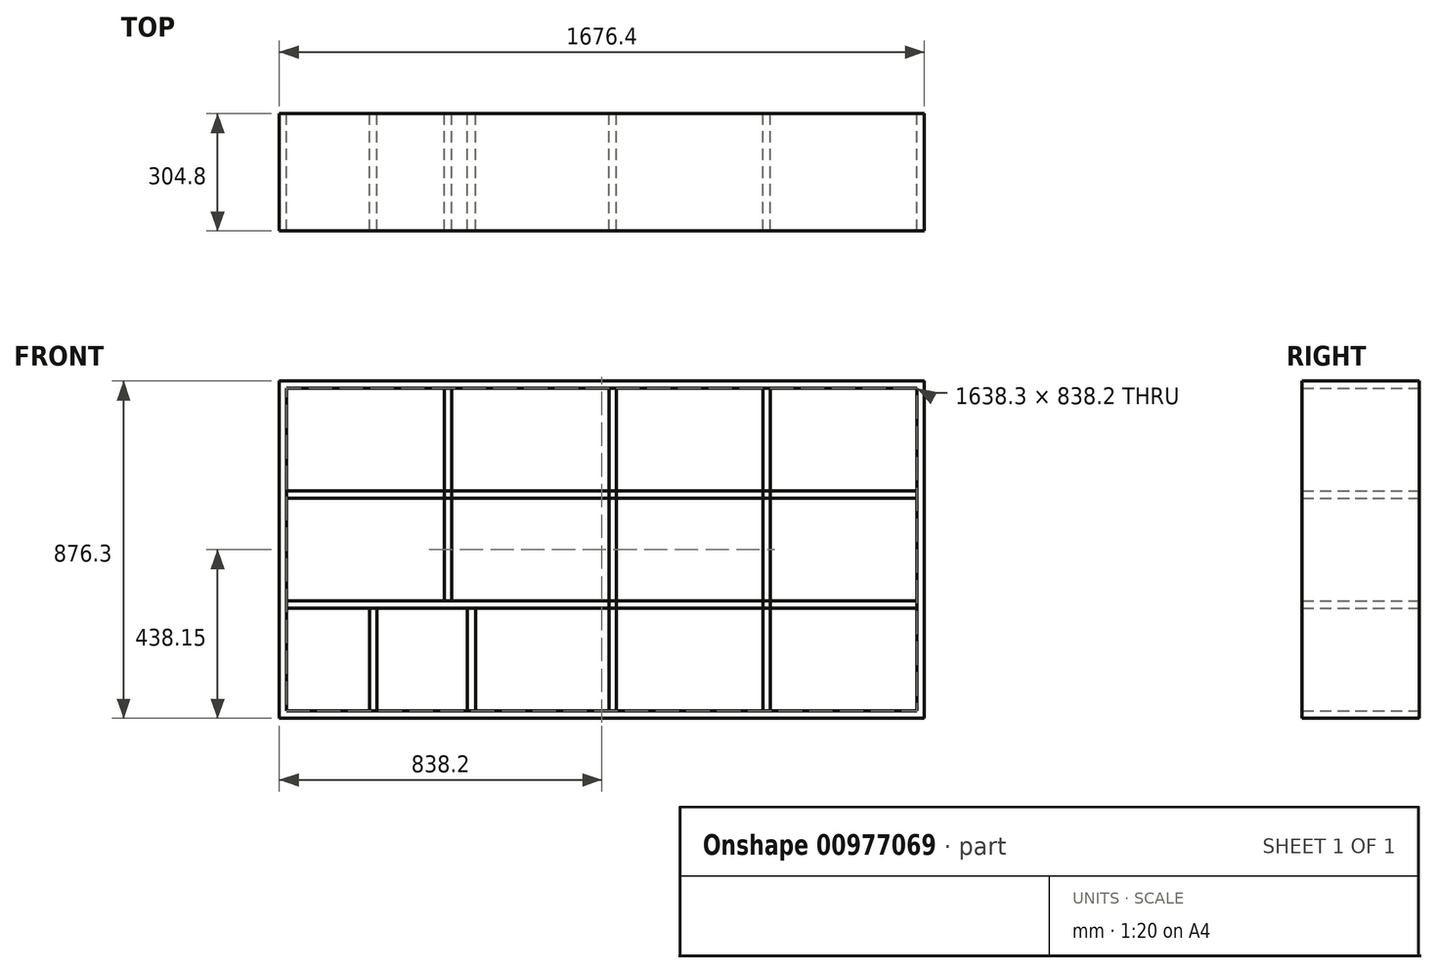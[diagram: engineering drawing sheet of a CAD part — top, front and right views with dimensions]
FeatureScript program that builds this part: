
annotation { "Feature Type Name" : "Feature", "Feature Type Description" : "" }
export const myFeature = defineFeature(function(context is Context, id is Id, definition is map)
    precondition{}
    {
        {
            var Q0;
            Q0=qCreatedBy(makeId("Front.planeOp"),FACE);
            var sketch = newSketch(context, id + "F0", { "sketchPlane" : qUnion([Q0])});
            skLineSegment(sketch, "E0.bottom", {"start": v(762, -381) * mm, "end": v(-762, -381) * mm});
            skLineSegment(sketch, "E0.top", {"start": v(762, 381) * mm, "end": v(-762, 381) * mm});
            skLineSegment(sketch, "E0.left", {"start": v(762, -381) * mm, "end": v(762, 381) * mm});
            skLineSegment(sketch, "E0.right", {"start": v(-762, -381) * mm, "end": v(-762, 381) * mm});
            skPoint(sketch, "E0.middle", {"position": v(0, 0) * mm});
            skLineSegment(sketch, "E1", {"start": v(-762, 127) * mm, "end": v(762, 127) * mm});
            skLineSegment(sketch, "E2", {"start": v(-762, -127) * mm, "end": v(762, -127) * mm});
            skLineSegment(sketch, "E3", {"start": v(-558.8, -381) * mm, "end": v(-558.8, -127) * mm});
            skLineSegment(sketch, "E4", {"start": v(-330.2, -127) * mm, "end": v(-330.2, -381) * mm});
            skLineSegment(sketch, "E5", {"start": v(381, -127) * mm, "end": v(381, -381) * mm});
            skLineSegment(sketch, "E6", {"start": v(0, -127) * mm, "end": v(0, -381) * mm});
            skLineSegment(sketch, "E7", {"start": v(-381, 127) * mm, "end": v(-381, -127) * mm});
            skLineSegment(sketch, "E8", {"start": v(0, 127) * mm, "end": v(0, -127) * mm});
            skLineSegment(sketch, "E9", {"start": v(381, -127) * mm, "end": v(381, 127) * mm});
            skLineSegment(sketch, "E10", {"start": v(-381, 127) * mm, "end": v(-381, 381) * mm});
            skLineSegment(sketch, "E11", {"start": v(0, 127) * mm, "end": v(0, 381) * mm});
            skLineSegment(sketch, "E12", {"start": v(381, 127) * mm, "end": v(381, 381) * mm});
            skSolve(sketch);
        }
        {
            var Q0;
            Q0=qCreatedBy(makeId("Front.planeOp"),FACE);
            var sketch = newSketch(context, id + "F1", { "sketchPlane" : qUnion([Q0])});
            skLineSegment(sketch, "E13.bottom", {"start": v(838.2, -438.15) * mm, "end": v(-838.2, -438.15) * mm});
            skLineSegment(sketch, "E13.top", {"start": v(838.2, 438.15) * mm, "end": v(-838.2, 438.15) * mm});
            skLineSegment(sketch, "E13.left", {"start": v(838.2, -438.15) * mm, "end": v(838.2, 438.15) * mm});
            skLineSegment(sketch, "E13.right", {"start": v(-838.2, -438.15) * mm, "end": v(-838.2, 438.15) * mm});
            skPoint(sketch, "E13.middle", {"position": v(0, 0) * mm});
            skSolve(sketch);
        }
        {
            var Q0;
            Q0=makeQuery(id+"F1.imprint","IMPRINT",FACE,{"disambiguationData":[TD([[makeQuery(id+"F1.imprint","IMPRINT",EDGE,{"derivedFrom":sQuery(id+"F1.wireOp",EDGE,"E13.bottom")}),-1.0]])]});
            extrude(context, id + "F2", {"entities" : qUnion([Q0]), "endBound" : BoundingType.SYMMETRIC, "depth" : 304.8 * mm, "offsetDistance" : 25.4 * mm});
        }
        {
            var Q0;
            Q0=makeQuery(id+"F2.opExtrude","CAP_FACE",FACE,{"disambiguationData":[OSD([sQuery(id+"F1.wireOp",EDGE,"E13.bottom"),sQuery(id+"F1.wireOp",EDGE,"E13.top"),sQuery(id+"F1.wireOp",EDGE,"E13.left"),sQuery(id+"F1.wireOp",EDGE,"E13.right")])],"isStart":false});
            var Q1;
            Q1=makeQuery(id+"F2.opExtrude","CAP_FACE",FACE,{"disambiguationData":[OSD([sQuery(id+"F1.wireOp",EDGE,"E13.bottom"),sQuery(id+"F1.wireOp",EDGE,"E13.top"),sQuery(id+"F1.wireOp",EDGE,"E13.left"),sQuery(id+"F1.wireOp",EDGE,"E13.right")])],"isStart":true});
            shell(context, id + "F3", {"entities" : qUnion([Q0, Q1]), "thickness" : 19.05 * mm});
        }
        {
            var Q0;
            Q0=makeQuery(id+"F2.opExtrude","CAP_FACE",FACE,{"disambiguationData":[OSD([sQuery(id+"F1.wireOp",EDGE,"E13.bottom"),sQuery(id+"F1.wireOp",EDGE,"E13.top"),sQuery(id+"F1.wireOp",EDGE,"E13.left"),sQuery(id+"F1.wireOp",EDGE,"E13.right")])],"isStart":true});
            var sketch = newSketch(context, id + "F4", { "sketchPlane" : qUnion([Q0])});
            skLineSegment(sketch, "E14", {"start": v(-438.15, 419.1) * mm, "end": v(-438.15, -419.1) * mm});
            skLineSegment(sketch, "E15", {"start": v(-438.15, -419.1) * mm, "end": v(-419.1, -419.1) * mm});
            skLineSegment(sketch, "E16", {"start": v(-419.1, -419.1) * mm, "end": v(-419.1, 419.1) * mm});
            skLineSegment(sketch, "E17", {"start": v(-419.1, 419.1) * mm, "end": v(-438.15, 419.1) * mm});
            skSolve(sketch);
        }
        {
            var Q0;
            Q0=makeQuery(id+"F4.imprint","IMPRINT",FACE,{"disambiguationData":[TD([[makeQuery(id+"F4.imprint","IMPRINT",EDGE,{"derivedFrom":sQuery(id+"F4.wireOp",EDGE,"E14")}),1.0]])]});
            extrude(context, id + "F5", {"entities" : qUnion([Q0]), "oppositeDirection" : true, "depth" : 304.8 * mm, "offsetDistance" : 25.4 * mm});
        }
        {
            var Q0;
            Q0=makeQuery(id+"F2.opExtrude","CAP_FACE",FACE,{"disambiguationData":[OSD([sQuery(id+"F1.wireOp",EDGE,"E13.bottom"),sQuery(id+"F1.wireOp",EDGE,"E13.top"),sQuery(id+"F1.wireOp",EDGE,"E13.left"),sQuery(id+"F1.wireOp",EDGE,"E13.right")])],"isStart":true});
            var sketch = newSketch(context, id + "F6", { "sketchPlane" : qUnion([Q0])});
            skLineSegment(sketch, "E18.bottom", {"start": v(-38.1, 419.1) * mm, "end": v(-19.05, 419.1) * mm});
            skLineSegment(sketch, "E18.top", {"start": v(-38.1, -419.1) * mm, "end": v(-19.05, -419.1) * mm});
            skLineSegment(sketch, "E18.left", {"start": v(-38.1, 419.1) * mm, "end": v(-38.1, -419.1) * mm});
            skLineSegment(sketch, "E18.right", {"start": v(-19.05, 419.1) * mm, "end": v(-19.05, -419.1) * mm});
            skSolve(sketch);
        }
        {
            var Q0;
            Q0=makeQuery(id+"F6.imprint","IMPRINT",FACE,{"disambiguationData":[TD([[makeQuery(id+"F6.imprint","IMPRINT",EDGE,{"derivedFrom":sQuery(id+"F6.wireOp",EDGE,"E18.bottom")}),-1.0]])]});
            extrude(context, id + "F7", {"entities" : qUnion([Q0]), "oppositeDirection" : true, "depth" : 304.8 * mm, "offsetDistance" : 25.4 * mm});
        }
        {
            var Q0;
            Q0=makeQuery(id+"F7.boolean.opBoolean","MERGE",FACE,{"derivedFrom":[makeQuery(id+"F2.opExtrude","CAP_FACE",FACE,{"disambiguationData":[OSD([sQuery(id+"F1.wireOp",EDGE,"E13.bottom"),sQuery(id+"F1.wireOp",EDGE,"E13.top"),sQuery(id+"F1.wireOp",EDGE,"E13.left"),sQuery(id+"F1.wireOp",EDGE,"E13.right")])],"isStart":true}),makeQuery(id+"F7.opExtrude","CAP_FACE",FACE,{"disambiguationData":[OSD([sQuery(id+"F6.wireOp",EDGE,"E18.bottom"),sQuery(id+"F6.wireOp",EDGE,"E18.top"),sQuery(id+"F6.wireOp",EDGE,"E18.left"),sQuery(id+"F6.wireOp",EDGE,"E18.right")])],"isStart":true})]});
            var sketch = newSketch(context, id + "F8", { "sketchPlane" : qUnion([Q0])});
            skLineSegment(sketch, "E19.bottom", {"start": v(-819.15, -152.4) * mm, "end": v(819.15, -152.4) * mm});
            skLineSegment(sketch, "E19.top", {"start": v(-819.15, -133.35) * mm, "end": v(819.15, -133.35) * mm});
            skLineSegment(sketch, "E19.left", {"start": v(-819.15, -152.4) * mm, "end": v(-819.15, -133.35) * mm});
            skLineSegment(sketch, "E19.right", {"start": v(819.15, -152.4) * mm, "end": v(819.15, -133.35) * mm});
            skLineSegment(sketch, "E20.bottom", {"start": v(-819.15, 133.35) * mm, "end": v(819.15, 133.35) * mm});
            skLineSegment(sketch, "E20.top", {"start": v(-819.15, 152.4) * mm, "end": v(819.15, 152.4) * mm});
            skLineSegment(sketch, "E20.left", {"start": v(-819.15, 133.35) * mm, "end": v(-819.15, 152.4) * mm});
            skLineSegment(sketch, "E20.right", {"start": v(819.15, 133.35) * mm, "end": v(819.15, 152.4) * mm});
            skSolve(sketch);
        }
        {
            var Q0;
            {var subQ0=sQuery(id+"F8.wireOp",EDGE,"E20.left");Q0=makeQuery(id+"F8.imprint","IMPRINT",FACE,{"disambiguationData":[TD([[makeQuery(id+"F8.imprint","IMPRINT",EDGE,{"derivedFrom":subQ0}),-1.0]])]});}
            var Q1;
            {var subQ0=sQuery(id+"F8.wireOp",EDGE,"E20.right");Q1=makeQuery(id+"F8.imprint","IMPRINT",FACE,{"disambiguationData":[TD([[makeQuery(id+"F8.imprint","IMPRINT",EDGE,{"derivedFrom":subQ0}),1.0]])]});}
            var Q2;
            {var subQ0=sQuery(id+"F8.wireOp",EDGE,"E20.bottom");var subQ1=makeQuery(id+"F7.opExtrude","CAP_EDGE",EDGE,{"disambiguationData":[OSD([sQuery(id+"F6.wireOp",EDGE,"E18.left")])],"isStart":true});var subQ2=makeQuery(id+"F8.imprint","INTERSECT",VERTEX,{"derivedFrom":[subQ1,subQ0]});Q2=makeQuery(id+"F8.imprint","IMPRINT",FACE,{"disambiguationData":[TD([[makeQuery(id+"F8.imprint","IMPRINT",EDGE,{"disambiguationData":[TD([[subQ2,-1.0]])],"derivedFrom":subQ0}),1.0]])]});}
            var Q3;
            {var subQ0=sQuery(id+"F8.wireOp",EDGE,"E19.left");Q3=makeQuery(id+"F8.imprint","IMPRINT",FACE,{"disambiguationData":[TD([[makeQuery(id+"F8.imprint","IMPRINT",EDGE,{"derivedFrom":subQ0}),-1.0]])]});}
            var Q4;
            {var subQ0=sQuery(id+"F8.wireOp",EDGE,"E19.bottom");var subQ1=makeQuery(id+"F7.opExtrude","CAP_EDGE",EDGE,{"disambiguationData":[OSD([sQuery(id+"F6.wireOp",EDGE,"E18.left")])],"isStart":true});var subQ2=makeQuery(id+"F8.imprint","INTERSECT",VERTEX,{"derivedFrom":[subQ1,subQ0]});Q4=makeQuery(id+"F8.imprint","IMPRINT",FACE,{"disambiguationData":[TD([[makeQuery(id+"F8.imprint","IMPRINT",EDGE,{"disambiguationData":[TD([[subQ2,-1.0]])],"derivedFrom":subQ0}),1.0]])]});}
            var Q5;
            {var subQ0=sQuery(id+"F8.wireOp",EDGE,"E19.right");Q5=makeQuery(id+"F8.imprint","IMPRINT",FACE,{"disambiguationData":[TD([[makeQuery(id+"F8.imprint","IMPRINT",EDGE,{"derivedFrom":subQ0}),1.0]])]});}
            extrude(context, id + "F9", {"entities" : qUnion([Q0, Q1, Q2, Q3, Q4, Q5]), "oppositeDirection" : true, "depth" : 304.8 * mm, "offsetDistance" : 25.4 * mm});
        }
        {
            var Q0;
            Q0=makeQuery(id+"F2.opExtrude","CAP_FACE",FACE,{"disambiguationData":[OSD([sQuery(id+"F1.wireOp",EDGE,"E13.bottom"),sQuery(id+"F1.wireOp",EDGE,"E13.top"),sQuery(id+"F1.wireOp",EDGE,"E13.left"),sQuery(id+"F1.wireOp",EDGE,"E13.right")])],"isStart":true});
            var sketch = newSketch(context, id + "F10", { "sketchPlane" : qUnion([Q0])});
            skLineSegment(sketch, "E21.bottom", {"start": v(390.54, 419.1) * mm, "end": v(409.6, 419.1) * mm});
            skLineSegment(sketch, "E21.top", {"start": v(390.54, -133.35) * mm, "end": v(409.6, -133.35) * mm});
            skLineSegment(sketch, "E21.left", {"start": v(390.54, 419.1) * mm, "end": v(390.54, -133.35) * mm});
            skLineSegment(sketch, "E21.right", {"start": v(409.6, 419.1) * mm, "end": v(409.6, -133.35) * mm});
            skLineSegment(sketch, "E22.bottom", {"start": v(327.99, -419.1) * mm, "end": v(349.25, -419.1) * mm});
            skLineSegment(sketch, "E22.top", {"start": v(327.99, -152.4) * mm, "end": v(349.25, -152.4) * mm});
            skLineSegment(sketch, "E22.left", {"start": v(327.99, -419.1) * mm, "end": v(327.99, -152.4) * mm});
            skLineSegment(sketch, "E22.right", {"start": v(349.25, -419.1) * mm, "end": v(349.25, -152.4) * mm});
            skLineSegment(sketch, "E23.bottom", {"start": v(584.2, -419.1) * mm, "end": v(603.25, -419.1) * mm});
            skLineSegment(sketch, "E23.top", {"start": v(584.2, -152.4) * mm, "end": v(603.25, -152.4) * mm});
            skLineSegment(sketch, "E23.left", {"start": v(584.2, -419.1) * mm, "end": v(584.2, -152.4) * mm});
            skLineSegment(sketch, "E23.right", {"start": v(603.25, -419.1) * mm, "end": v(603.25, -152.4) * mm});
            skSolve(sketch);
        }
        {
            var Q0;
            Q0=makeQuery(id+"F10.imprint","IMPRINT",FACE,{"disambiguationData":[TD([[makeQuery(id+"F10.imprint","IMPRINT",EDGE,{"derivedFrom":sQuery(id+"F10.wireOp",EDGE,"E21.bottom")}),-1.0]])]});
            var Q1;
            Q1=makeQuery(id+"F10.imprint","IMPRINT",FACE,{"disambiguationData":[TD([[makeQuery(id+"F10.imprint","IMPRINT",EDGE,{"derivedFrom":sQuery(id+"F10.wireOp",EDGE,"E22.bottom")}),1.0]])]});
            var Q2;
            Q2=makeQuery(id+"F10.imprint","IMPRINT",FACE,{"disambiguationData":[TD([[makeQuery(id+"F10.imprint","IMPRINT",EDGE,{"derivedFrom":sQuery(id+"F10.wireOp",EDGE,"E23.bottom")}),1.0]])]});
            extrude(context, id + "F11", {"entities" : qUnion([Q0, Q1, Q2]), "oppositeDirection" : true, "depth" : 304.8 * mm, "offsetDistance" : 25.4 * mm});
        }
    });
